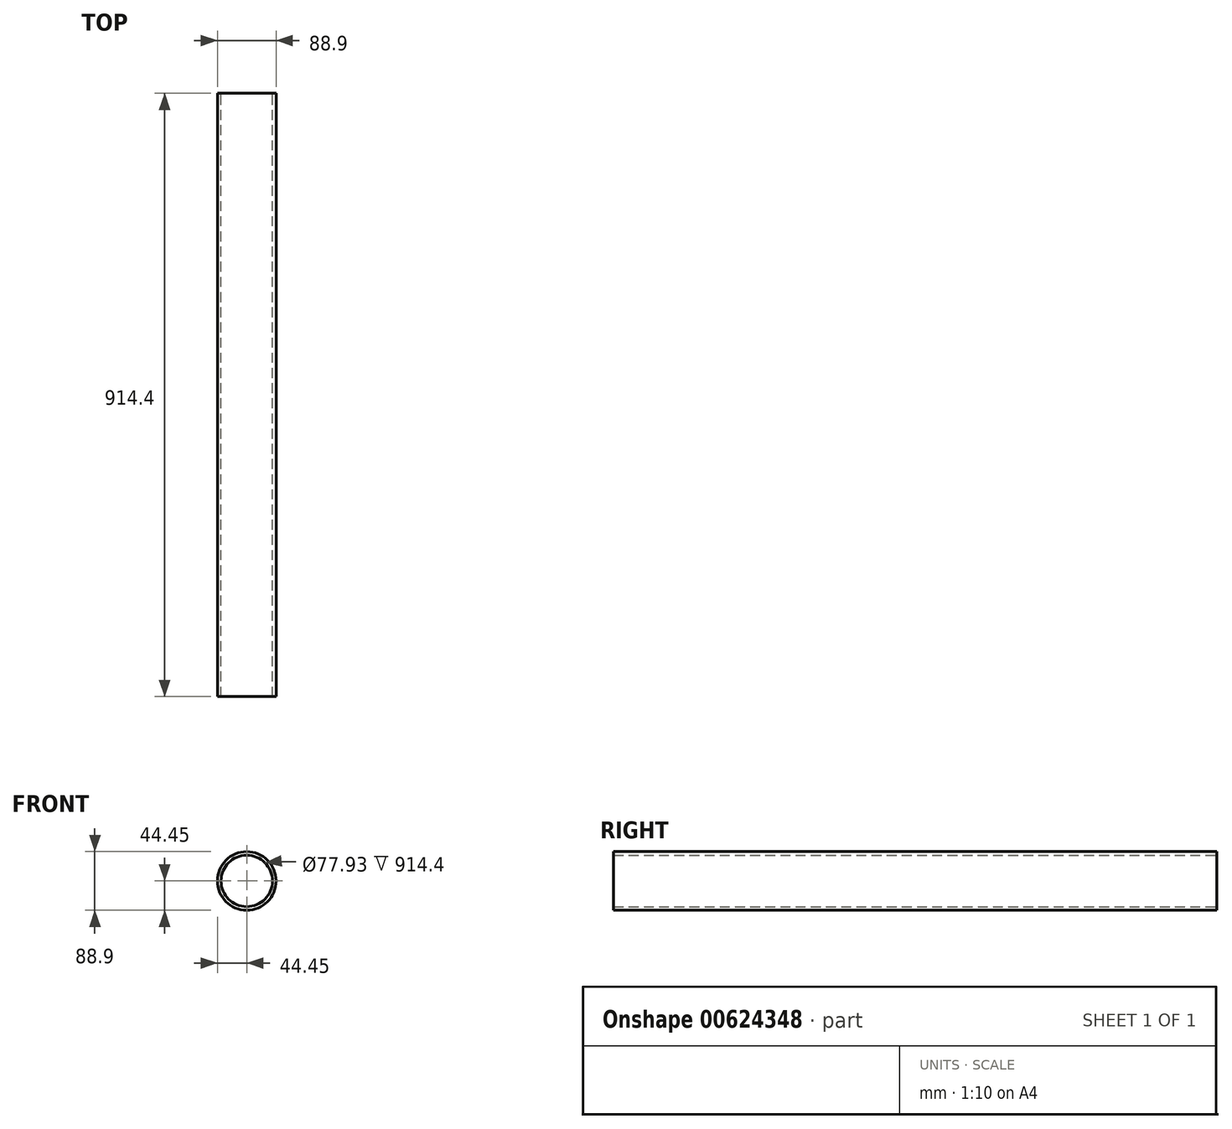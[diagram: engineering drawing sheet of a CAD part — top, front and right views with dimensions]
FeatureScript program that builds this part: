
annotation { "Feature Type Name" : "Feature", "Feature Type Description" : "" }
export const myFeature = defineFeature(function(context is Context, id is Id, definition is map)
    precondition{}
    {
        {
            var Q0;
            Q0=qCreatedBy(makeId("Front.planeOp"),FACE);
            var sketch = newSketch(context, id + "F0", { "sketchPlane" : qUnion([Q0])});
            skCircle(sketch, "E0", {"center": v(0, 0) * mm, "radius": 38.96 * mm});
            skCircle(sketch, "E1", {"center": v(0, 0) * mm, "radius": 44.45 * mm});
            skSolve(sketch);
        }
        {
            var Q0;
            Q0=makeQuery(id+"F0.imprint","IMPRINT",FACE,{"disambiguationData":[TD([[makeQuery(id+"F0.imprint","IMPRINT",EDGE,{"derivedFrom":sQuery(id+"F0.wireOp",EDGE,"E0")}),-1.0]])]});
            extrude(context, id + "F1", {"entities" : qUnion([Q0]), "depth" : 914.4 * mm, "offsetDistance" : 25.4 * mm});
        }
    });
